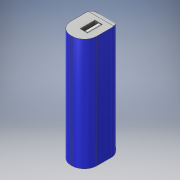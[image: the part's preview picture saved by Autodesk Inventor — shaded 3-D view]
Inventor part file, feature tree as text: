
AUTODESK INVENTOR PART (.ipt)
format: ipt  version: 2018 (Build 220112000, 112)  size: 179,200 bytes
history: native  units: in
note: dims shown in document units (in); Inventor stores cm internally (conversion verified against a paired STEP export)
features: sketch x5, extrude x4, fillet x2
ambient origin geometry x8: Origin, YZ Plane, XZ Plane, XY Plane, X Axis, Y Axis, Z Axis, Center Point
bodies: Solid1 (feature_tree)
feature tree (11):
  extrude  "Extrusion1"  Depth=0.8268in
  fillet  "Fillet1"  Radius=3.5827in
  fillet  "Fillet2"  Radius=0.3937in
  extrude  "Extrusion3"  Depth=0.8268in
  sketch  "Sketch3"  dims[d11=0.315in d12=0.2362in]
  sketch  "Sketch4"  dims[d20=0.315in d21=0.2362in]
  extrude  "Extrusion4"  Depth=0.2362in
  extrude  "Extrusion5"  Depth=0.2362in
  sketch  "Sketch5"  dims[d22=3.5827in d23=0.0in d24=0.2362in d25=0.4724in d26=0.2362in d27=0.3346in d28=0.0787in d29=0.4331in d30=0.2559in d31=0.3543in d32=0.3937in d33=0.0in d34=0.3937in d35=0.0in]
  sketch  "Sketch1"  dims[d4=1.1811in d5=0.8268in d6=3.5827in d7=0.0in d8=0.3937in]
  sketch  "Sketch2"  dims[d9=0.2362in d10=0.8268in]
